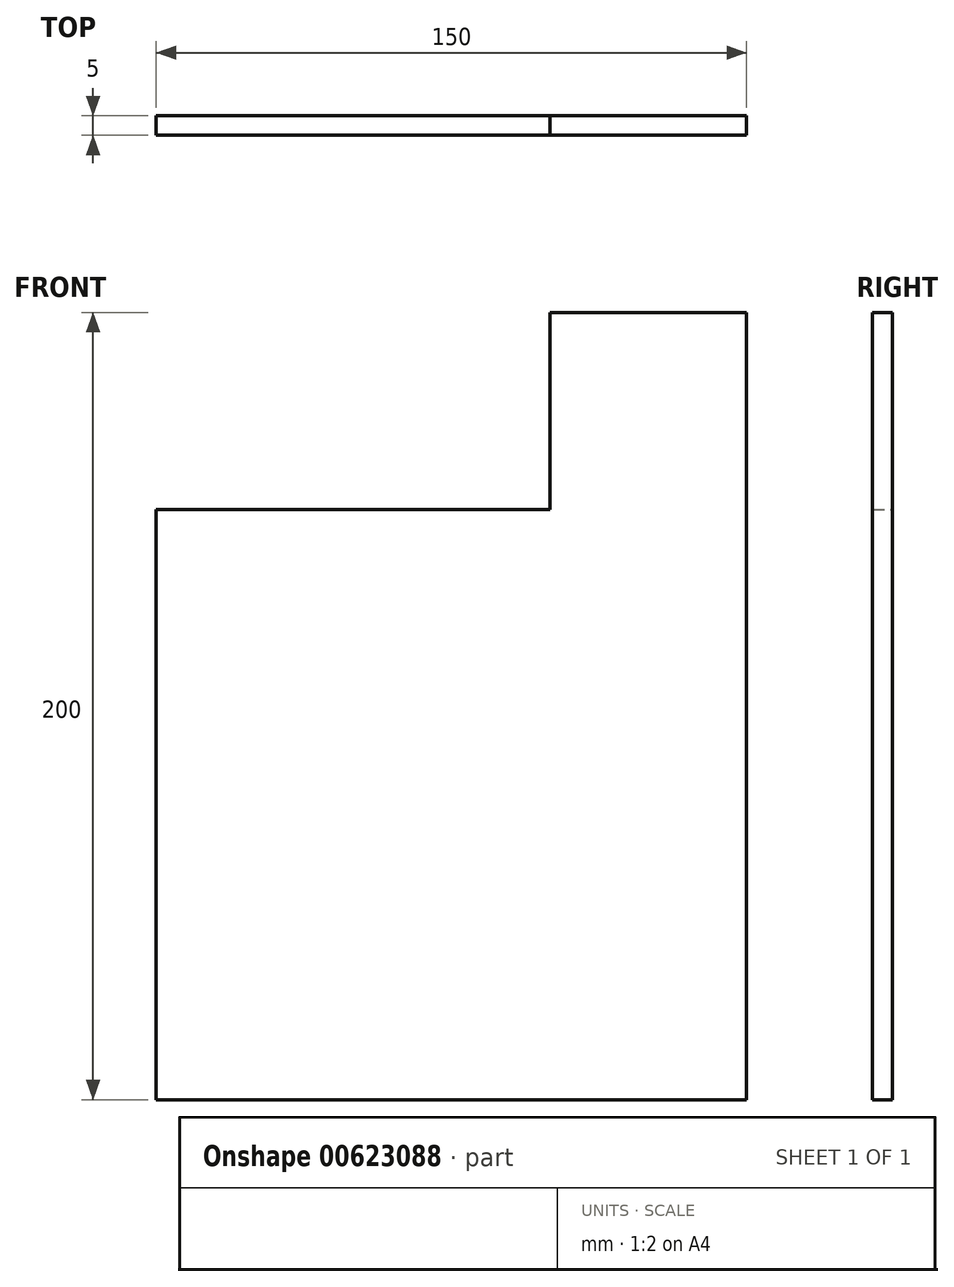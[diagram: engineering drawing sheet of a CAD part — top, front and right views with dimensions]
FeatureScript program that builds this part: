
annotation { "Feature Type Name" : "Feature", "Feature Type Description" : "" }
export const myFeature = defineFeature(function(context is Context, id is Id, definition is map)
    precondition{}
    {
        {
            var Q0;
            Q0=qCreatedBy(makeId("Front.planeOp"),FACE);
            var sketch = newSketch(context, id + "F0", { "sketchPlane" : qUnion([Q0])});
            skLineSegment(sketch, "E0", {"start": v(-150, 150) * mm, "end": v(-150, 0) * mm});
            skLineSegment(sketch, "E1", {"start": v(-150, 150) * mm, "end": v(-50, 150) * mm});
            skLineSegment(sketch, "E2", {"start": v(-50, 200) * mm, "end": v(0, 200) * mm});
            skLineSegment(sketch, "E3", {"start": v(0, 200) * mm, "end": v(0, 0) * mm});
            skLineSegment(sketch, "E4", {"start": v(0, 0) * mm, "end": v(-150, 0) * mm});
            skLineSegment(sketch, "E5", {"start": v(-50, 150) * mm, "end": v(-50, 200) * mm});
            skSolve(sketch);
        }
        {
            var Q0;
            Q0=makeQuery(id+"F0.imprint","IMPRINT",FACE,{"disambiguationData":[TD([[makeQuery(id+"F0.imprint","IMPRINT",EDGE,{"derivedFrom":sQuery(id+"F0.wireOp",EDGE,"E0")}),1.0]])]});
            extrude(context, id + "F1", {"entities" : qUnion([Q0]), "depth" : 5 * mm, "offsetDistance" : 25 * mm});
        }
    });
